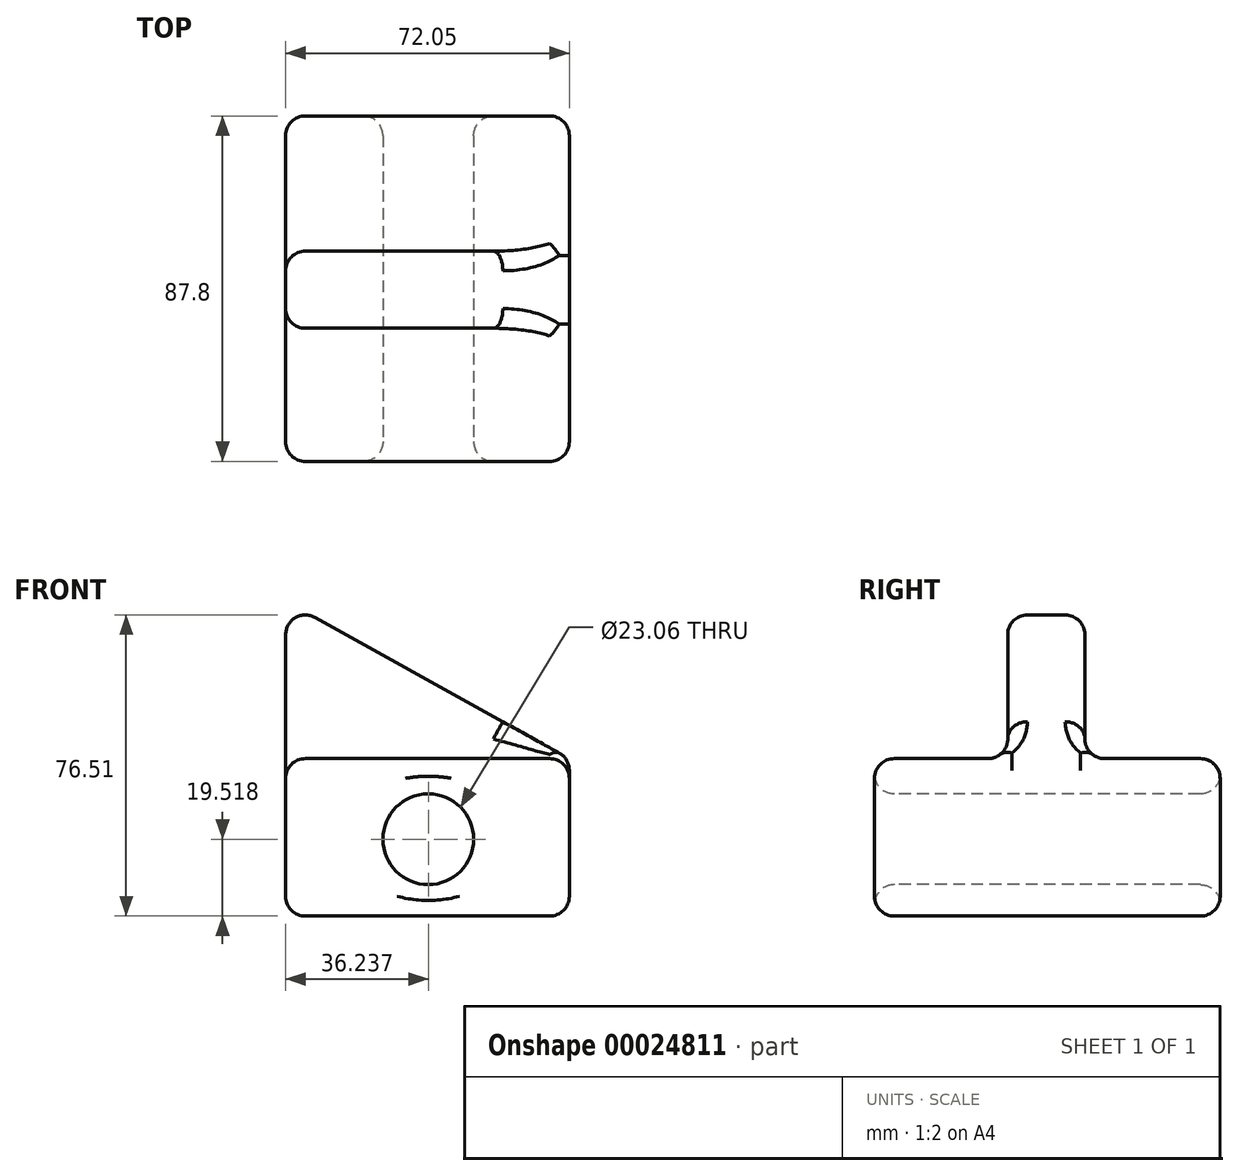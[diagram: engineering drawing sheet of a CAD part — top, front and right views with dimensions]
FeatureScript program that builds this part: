
annotation { "Feature Type Name" : "Feature", "Feature Type Description" : "" }
export const myFeature = defineFeature(function(context is Context, id is Id, definition is map)
    precondition{}
    {
        {
            var Q0;
            Q0=qCreatedBy(makeId("Top.planeOp"),FACE);
            var sketch = newSketch(context, id + "F0", { "sketchPlane" : qUnion([Q0])});
            skLineSegment(sketch, "E0.bottom", {"start": v(-59.89, -44.54) * mm, "end": v(12.16, -44.54) * mm});
            skLineSegment(sketch, "E0.top", {"start": v(-59.89, 43.26) * mm, "end": v(12.16, 43.26) * mm});
            skLineSegment(sketch, "E0.left", {"start": v(-59.89, -44.54) * mm, "end": v(-59.89, 43.26) * mm});
            skLineSegment(sketch, "E0.right", {"start": v(12.16, -44.54) * mm, "end": v(12.16, 43.26) * mm});
            skSolve(sketch);
        }
        {
            var Q0;
            Q0=makeQuery(id+"F0.imprint","IMPRINT",FACE,{"disambiguationData":[TD([[makeQuery(id+"F0.imprint","IMPRINT",EDGE,{"derivedFrom":sQuery(id+"F0.wireOp",EDGE,"E0.bottom")}),1.0]])]});
            extrude(context, id + "F1", {"entities" : qUnion([Q0]), "depth" : 40 * mm});
        }
        {
            var Q0;
            Q0=makeQuery(id+"F1.opExtrude","SWEPT_FACE",FACE,{"disambiguationData":[OSD([sQuery(id+"F0.wireOp",EDGE,"E0.bottom")])]});
            var sketch = newSketch(context, id + "F2", { "sketchPlane" : qUnion([Q0])});
            skCircle(sketch, "E1", {"center": v(-23.65, 19.52) * mm, "radius": 11.53 * mm});
            skSolve(sketch);
        }
        {
            var Q0;
            Q0=makeQuery(id+"F2.imprint","IMPRINT",FACE,{"disambiguationData":[TD([[makeQuery(id+"F2.imprint","IMPRINT",EDGE,{"derivedFrom":sQuery(id+"F2.wireOp",EDGE,"E1")}),1.0]])]});
            extrude(context, id + "F3", {"entities" : qUnion([Q0]), "operationType" : NewBodyOperationType.REMOVE, "endBound" : BoundingType.THROUGH_ALL, "oppositeDirection" : true, "depth" : 25 * mm});
        }
        {
            var Q0;
            Q0=makeQuery(id+"F1.opExtrude","CAP_FACE",FACE,{"disambiguationData":[OSD([sQuery(id+"F0.wireOp",EDGE,"E0.bottom"),sQuery(id+"F0.wireOp",EDGE,"E0.top"),sQuery(id+"F0.wireOp",EDGE,"E0.left"),sQuery(id+"F0.wireOp",EDGE,"E0.right")])],"isStart":false});
            var sketch = newSketch(context, id + "F4", { "sketchPlane" : qUnion([Q0])});
            skLineSegment(sketch, "E2.bottom", {"start": v(-59.89, -10.7) * mm, "end": v(12.16, -10.7) * mm});
            skLineSegment(sketch, "E2.top", {"start": v(-59.89, 8.88) * mm, "end": v(12.16, 8.88) * mm});
            skLineSegment(sketch, "E2.left", {"start": v(-59.89, -10.7) * mm, "end": v(-59.89, 8.88) * mm});
            skLineSegment(sketch, "E2.right", {"start": v(12.16, -10.7) * mm, "end": v(12.16, 8.88) * mm});
            skSolve(sketch);
        }
        {
            var Q0;
            Q0=makeQuery(id+"F4.imprint","IMPRINT",FACE,{"disambiguationData":[TD([[makeQuery(id+"F4.imprint","IMPRINT",EDGE,{"derivedFrom":sQuery(id+"F4.wireOp",EDGE,"E2.bottom")}),1.0]])]});
            extrude(context, id + "F5", {"entities" : qUnion([Q0]), "operationType" : NewBodyOperationType.ADD, "depth" : 40 * mm});
        }
        {
            var Q0;
            Q0=makeQuery(id+"F5.opExtrude","SWEPT_FACE",FACE,{"disambiguationData":[OSD([sQuery(id+"F4.wireOp",EDGE,"E2.bottom")])]});
            var sketch = newSketch(context, id + "F6", { "sketchPlane" : qUnion([Q0])});
            skLineSegment(sketch, "E3", {"start": v(12.16, 40) * mm, "end": v(-59.89, 80) * mm});
            skSolve(sketch);
        }
        {
            var Q0;
            Q0=makeQuery(id+"F6.imprint","IMPRINT",FACE,{"disambiguationData":[TD([[makeQuery(id+"F6.imprint","IMPRINT",EDGE,{"derivedFrom":sQuery(id+"F6.wireOp",EDGE,"E3")}),-1.0]])]});
            extrude(context, id + "F7", {"entities" : qUnion([Q0]), "operationType" : NewBodyOperationType.REMOVE, "endBound" : BoundingType.THROUGH_ALL, "oppositeDirection" : true, "depth" : 25 * mm});
        }
        {
            var Q0;
            Q0=makeQuery(id+"F1.opExtrude","SWEPT_FACE",FACE,{"disambiguationData":[OSD([sQuery(id+"F0.wireOp",EDGE,"E0.bottom")])]});
            var Q1;
            {var subQ0=sQuery(id+"F0.wireOp",EDGE,"E0.bottom");var subQ1=sQuery(id+"F0.wireOp",EDGE,"E0.left");var subQ2=sQuery(id+"F0.wireOp",EDGE,"E0.right");Q1=makeQuery(id+"F5.boolean.opBoolean","SPLIT",FACE,{"disambiguationData":[TD([makeQuery(id+"F1.opExtrude","SWEPT_FACE",FACE,{"disambiguationData":[OSD([subQ0])]})])],"derivedFrom":makeQuery(id+"F1.opExtrude","CAP_FACE",FACE,{"disambiguationData":[OSD([subQ0,sQuery(id+"F0.wireOp",EDGE,"E0.top"),subQ1,subQ2])],"isStart":false})});}
            var Q2;
            Q2=makeQuery(id+"F5.boolean.opBoolean","MERGE",FACE,{"derivedFrom":[makeQuery(id+"F1.opExtrude","SWEPT_FACE",FACE,{"disambiguationData":[OSD([sQuery(id+"F0.wireOp",EDGE,"E0.right")])]}),makeQuery(id+"F5.opExtrude","SWEPT_FACE",FACE,{"disambiguationData":[OSD([sQuery(id+"F4.wireOp",EDGE,"E2.right")])]})]});
            var Q3;
            Q3=makeQuery(id+"F7.boolean.opBoolean","COPY",FACE,{"derivedFrom":makeQuery(id+"F7.opExtrude","SWEPT_FACE",FACE,{"disambiguationData":[OSD([sQuery(id+"F6.wireOp",EDGE,"E3")])]})});
            var Q4;
            Q4=makeQuery(id+"F5.opExtrude","SWEPT_FACE",FACE,{"disambiguationData":[OSD([sQuery(id+"F4.wireOp",EDGE,"E2.bottom")])]});
            var Q5;
            {var subQ0=sQuery(id+"F0.wireOp",EDGE,"E0.top");var subQ1=sQuery(id+"F0.wireOp",EDGE,"E0.left");var subQ2=sQuery(id+"F0.wireOp",EDGE,"E0.right");Q5=makeQuery(id+"F5.boolean.opBoolean","SPLIT",FACE,{"disambiguationData":[TD([makeQuery(id+"F1.opExtrude","SWEPT_FACE",FACE,{"disambiguationData":[OSD([subQ0])]})])],"derivedFrom":makeQuery(id+"F1.opExtrude","CAP_FACE",FACE,{"disambiguationData":[OSD([sQuery(id+"F0.wireOp",EDGE,"E0.bottom"),subQ0,subQ1,subQ2])],"isStart":false})});}
            var Q6;
            Q6=makeQuery(id+"F1.opExtrude","SWEPT_FACE",FACE,{"disambiguationData":[OSD([sQuery(id+"F0.wireOp",EDGE,"E0.top")])]});
            var Q7;
            Q7=makeQuery(id+"F5.boolean.opBoolean","MERGE",FACE,{"derivedFrom":[makeQuery(id+"F1.opExtrude","SWEPT_FACE",FACE,{"disambiguationData":[OSD([sQuery(id+"F0.wireOp",EDGE,"E0.left")])]}),makeQuery(id+"F5.opExtrude","SWEPT_FACE",FACE,{"disambiguationData":[OSD([sQuery(id+"F4.wireOp",EDGE,"E2.left")])]})]});
            fillet(context, id + "F8", {"entities" : qUnion([Q0, Q1, Q2, Q3, Q4, Q5, Q6, Q7]), "radius" : 5 * mm, "tangentPropagation" : true, "allowEdgeOverflow" : false});
        }
    });
